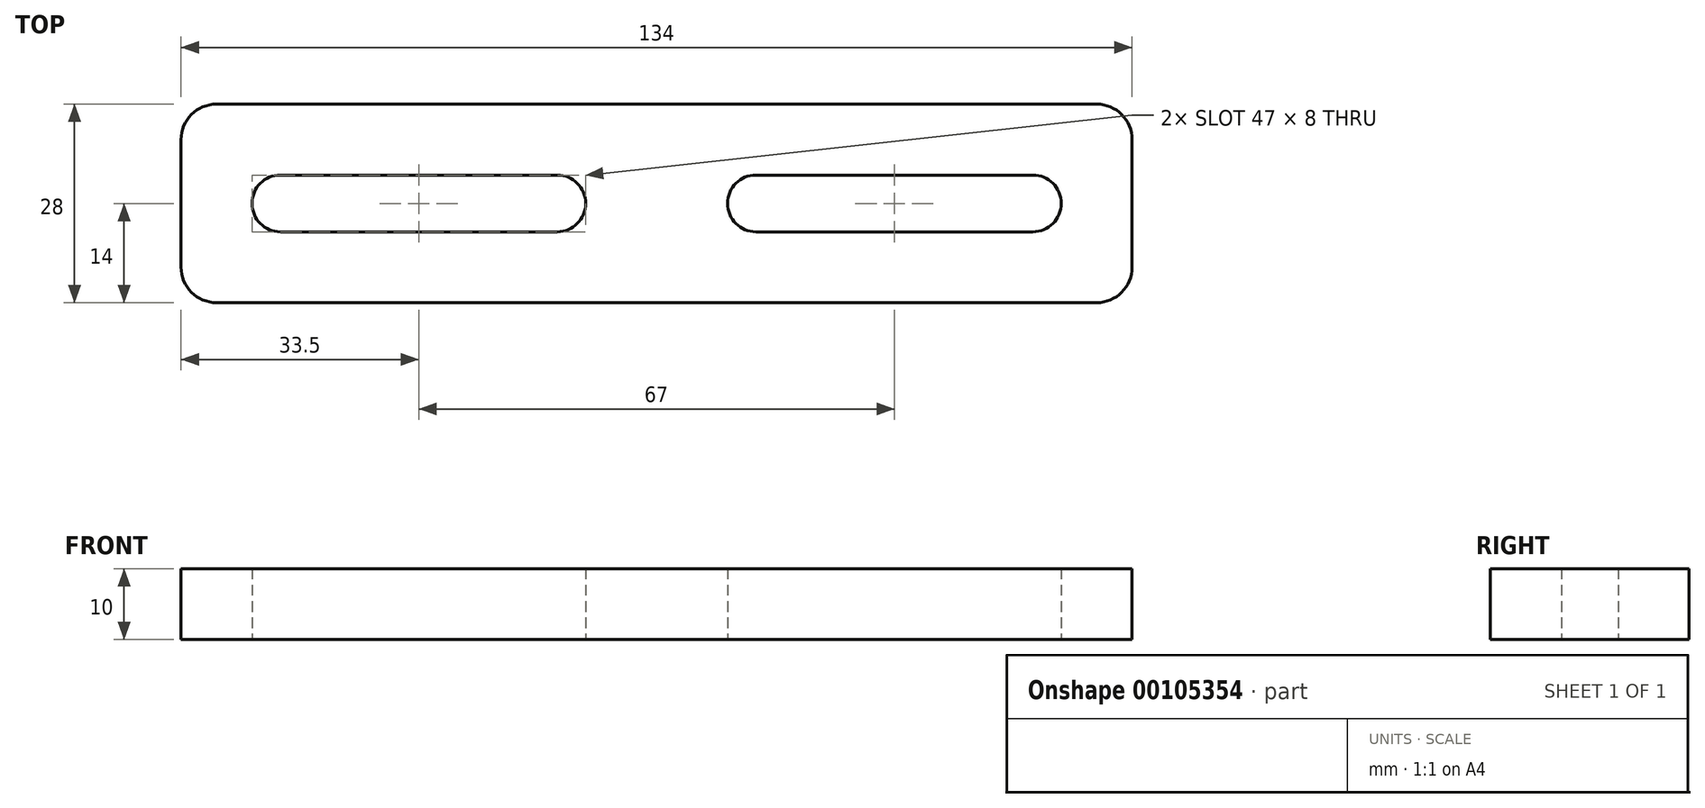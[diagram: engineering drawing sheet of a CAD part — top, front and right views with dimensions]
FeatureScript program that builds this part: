
annotation { "Feature Type Name" : "Feature", "Feature Type Description" : "" }
export const myFeature = defineFeature(function(context is Context, id is Id, definition is map)
    precondition{}
    {
        {
            var Q0;
            Q0=qCreatedBy(makeId("Top.planeOp"),FACE);
            var sketch = newSketch(context, id + "F0", { "sketchPlane" : qUnion([Q0])});
            skArc(sketch, "E0", {"start": v(0, 4) * mm, "mid": v(-4, 0) * mm, "end": v(0, -4) * mm});
            skArc(sketch, "E1", {"start": v(39, -4) * mm, "mid": v(43, 0) * mm, "end": v(39, 4) * mm});
            skLineSegment(sketch, "E2", {"start": v(0, 4) * mm, "end": v(39, 4) * mm});
            skLineSegment(sketch, "E3", {"start": v(0, -4) * mm, "end": v(39, -4) * mm});
            skLineSegment(sketch, "E4.bottom", {"start": v(-14, 14) * mm, "end": v(53, 14) * mm});
            skLineSegment(sketch, "E4.top", {"start": v(-14, -14) * mm, "end": v(53, -14) * mm});
            skLineSegment(sketch, "E4.left", {"start": v(-14, 14) * mm, "end": v(-14, -14) * mm});
            skLineSegment(sketch, "E4.right", {"start": v(53, 14) * mm, "end": v(53, -14) * mm, "construction": true});
            skLineSegment(sketch, "E5", {"start": v(19.5, 4) * mm, "end": v(19.5, -4) * mm, "construction": true});
            skArc(sketch, "E6.MirrorCS", {"start": v(106, 4) * mm, "mid": v(110, 0) * mm, "end": v(106, -4) * mm});
            skArc(sketch, "E7.MirrorCS", {"start": v(67, -4) * mm, "mid": v(63, 0) * mm, "end": v(67, 4) * mm});
            skLineSegment(sketch, "E8.MirrorCS", {"start": v(106, 4) * mm, "end": v(67, 4) * mm});
            skLineSegment(sketch, "E9.MirrorCS", {"start": v(86.5, 4) * mm, "end": v(86.5, -4) * mm, "construction": true});
            skLineSegment(sketch, "E10.MirrorCS", {"start": v(106, -4) * mm, "end": v(67, -4) * mm});
            skLineSegment(sketch, "E11.MirrorCS", {"start": v(120, 14) * mm, "end": v(120, -14) * mm});
            skLineSegment(sketch, "E12.MirrorCS", {"start": v(120, 14) * mm, "end": v(53, 14) * mm});
            skLineSegment(sketch, "E13.MirrorCS", {"start": v(120, -14) * mm, "end": v(53, -14) * mm});
            skSolve(sketch);
        }
        {
            var Q0;
            Q0 = qSketchRegion(id + "F0", true);
            extrude(context, id + "F1", {"entities" : qUnion([Q0]), "depth" : 10 * mm});
        }
        {
            var Q0;
            Q0=makeQuery(id+"F1.opExtrude","SWEPT_EDGE",EDGE,{"disambiguationData":[OSD([sQuery(id+"F0.wireOp",EDGE,"E4.bottom"),sQuery(id+"F0.wireOp",EDGE,"E4.left")])]});
            var Q1;
            Q1=makeQuery(id+"F1.opExtrude","SWEPT_EDGE",EDGE,{"disambiguationData":[OSD([sQuery(id+"F0.wireOp",EDGE,"E4.top"),sQuery(id+"F0.wireOp",EDGE,"E4.left")])]});
            var Q2;
            Q2=makeQuery(id+"F1.opExtrude","SWEPT_EDGE",EDGE,{"disambiguationData":[OSD([sQuery(id+"F0.wireOp",EDGE,"E11.MirrorCS"),sQuery(id+"F0.wireOp",EDGE,"E13.MirrorCS")])]});
            var Q3;
            Q3=makeQuery(id+"F1.opExtrude","SWEPT_EDGE",EDGE,{"disambiguationData":[OSD([sQuery(id+"F0.wireOp",EDGE,"E11.MirrorCS"),sQuery(id+"F0.wireOp",EDGE,"E12.MirrorCS")])]});
            fillet(context, id + "F2", {"entities" : qUnion([Q0, Q1, Q2, Q3]), "radius" : 5 * mm, "tangentPropagation" : true, "allowEdgeOverflow" : false});
        }
    });
